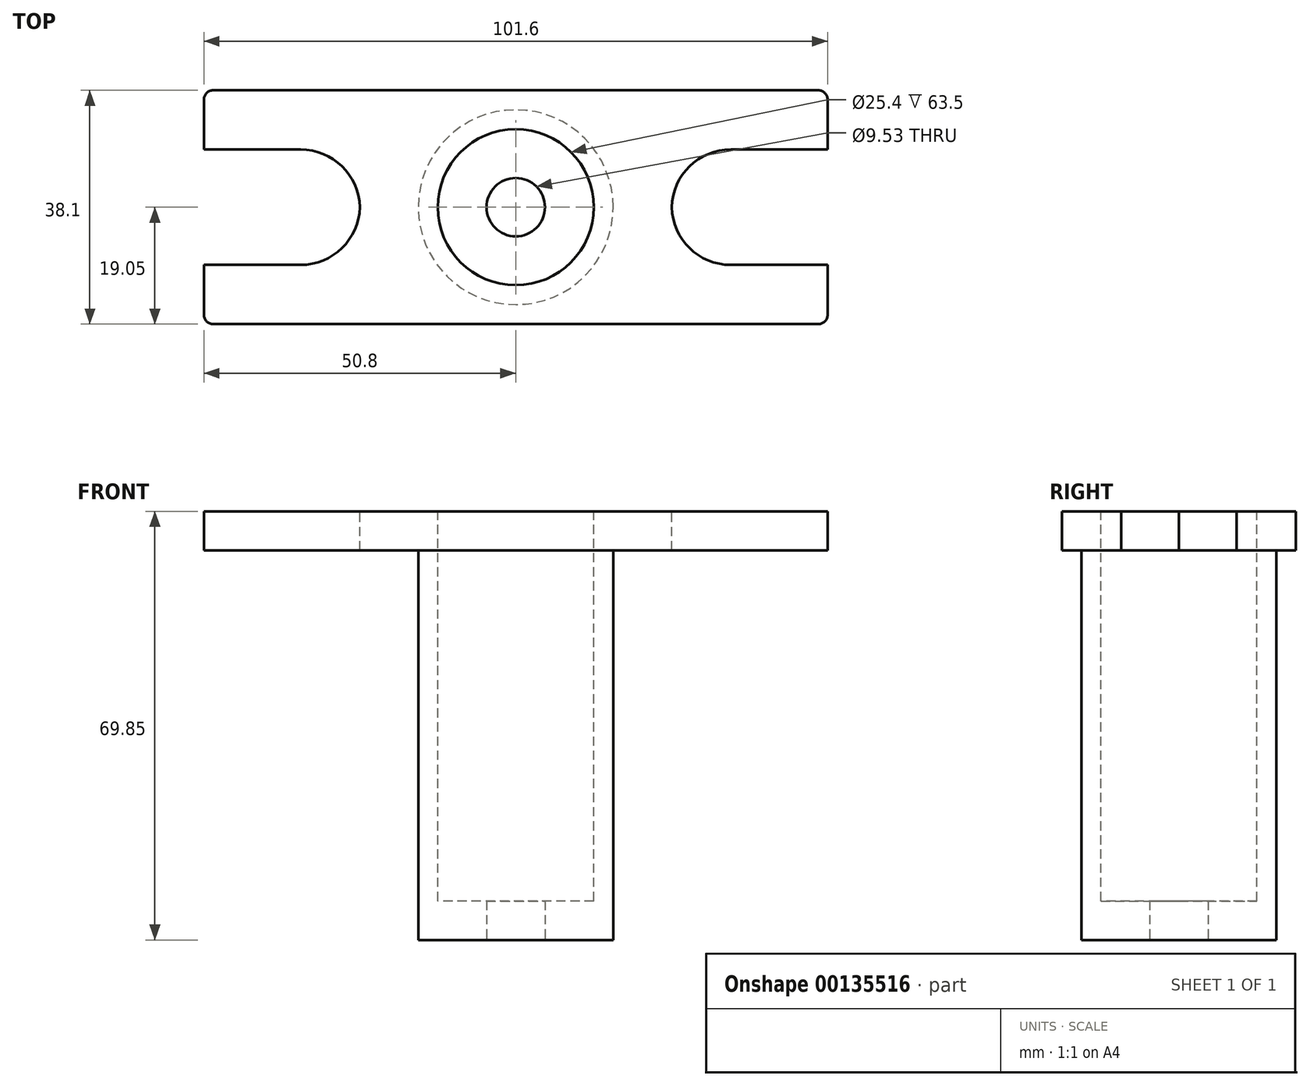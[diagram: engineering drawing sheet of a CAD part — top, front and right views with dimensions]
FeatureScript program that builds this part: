
annotation { "Feature Type Name" : "Feature", "Feature Type Description" : "" }
export const myFeature = defineFeature(function(context is Context, id is Id, definition is map)
    precondition{}
    {
        {
            var Q0;
            Q0=qCreatedBy(makeId("Top.planeOp"),FACE);
            var sketch = newSketch(context, id + "F0", { "sketchPlane" : qUnion([Q0])});
            skCircle(sketch, "E0", {"center": v(0, 0) * mm, "radius": 12.7 * mm});
            skLineSegment(sketch, "E1", {"start": v(49.28, 19.05) * mm, "end": v(-49.28, 19.05) * mm});
            skLineSegment(sketch, "E2", {"start": v(-50.8, 17.53) * mm, "end": v(-50.8, 9.4) * mm});
            skLineSegment(sketch, "E3", {"start": v(-50.8, 9.4) * mm, "end": v(-35.05, 9.4) * mm});
            skLineSegment(sketch, "E4", {"start": v(-25.4, 0) * mm, "end": v(-25.4, -0.25) * mm});
            skLineSegment(sketch, "E5", {"start": v(-25.4, 0.25) * mm, "end": v(-25.4, 0) * mm});
            skLineSegment(sketch, "E6", {"start": v(-35.05, -9.4) * mm, "end": v(-50.8, -9.4) * mm});
            skLineSegment(sketch, "E7", {"start": v(-50.8, -9.4) * mm, "end": v(-50.8, -17.53) * mm});
            skLineSegment(sketch, "E8", {"start": v(-49.28, -19.05) * mm, "end": v(49.28, -19.05) * mm});
            skLineSegment(sketch, "E9", {"start": v(50.8, -17.53) * mm, "end": v(50.8, -9.4) * mm});
            skLineSegment(sketch, "E10", {"start": v(50.8, -9.4) * mm, "end": v(35.05, -9.4) * mm});
            skLineSegment(sketch, "E11", {"start": v(25.4, -0.25) * mm, "end": v(25.4, 0.25) * mm});
            skLineSegment(sketch, "E12", {"start": v(35.05, 9.4) * mm, "end": v(50.8, 9.4) * mm});
            skLineSegment(sketch, "E13", {"start": v(50.8, 9.4) * mm, "end": v(50.8, 17.53) * mm});
            skPoint(sketch, "E14", {"position": v(25.4, 0) * mm});
            skPoint(sketch, "E15.visualSharp", {"position": v(-25.4, 9.4) * mm});
            skArc(sketch, "E15.filletArc", {"start": v(-25.4, -0.25) * mm, "mid": v(-28.23, 6.57) * mm, "end": v(-35.05, 9.4) * mm});
            skPoint(sketch, "E16.visualSharp", {"position": v(-25.4, -9.4) * mm});
            skArc(sketch, "E16.filletArc", {"start": v(-35.05, -9.4) * mm, "mid": v(-28.23, -6.57) * mm, "end": v(-25.4, 0.25) * mm});
            skPoint(sketch, "E17.visualSharp", {"position": v(25.4, 9.4) * mm});
            skArc(sketch, "E17.filletArc", {"start": v(35.05, 9.4) * mm, "mid": v(28.23, 6.57) * mm, "end": v(25.4, -0.25) * mm});
            skPoint(sketch, "E18.visualSharp", {"position": v(25.4, -9.4) * mm});
            skArc(sketch, "E18.filletArc", {"start": v(25.4, 0.25) * mm, "mid": v(28.23, -6.57) * mm, "end": v(35.05, -9.4) * mm});
            skPoint(sketch, "E19.visualSharp", {"position": v(50.8, 19.05) * mm});
            skArc(sketch, "E19.filletArc", {"start": v(50.8, 17.53) * mm, "mid": v(50.35, 18.6) * mm, "end": v(49.28, 19.05) * mm});
            skPoint(sketch, "E20.visualSharp", {"position": v(50.8, -19.05) * mm});
            skArc(sketch, "E20.filletArc", {"start": v(49.28, -19.05) * mm, "mid": v(50.35, -18.6) * mm, "end": v(50.8, -17.53) * mm});
            skPoint(sketch, "E21.visualSharp", {"position": v(-50.8, -19.05) * mm});
            skArc(sketch, "E21.filletArc", {"start": v(-50.8, -17.53) * mm, "mid": v(-50.35, -18.6) * mm, "end": v(-49.28, -19.05) * mm});
            skPoint(sketch, "E22.visualSharp", {"position": v(-50.8, 19.05) * mm});
            skArc(sketch, "E22.filletArc", {"start": v(-49.28, 19.05) * mm, "mid": v(-50.35, 18.6) * mm, "end": v(-50.8, 17.53) * mm});
            skSolve(sketch);
        }
        {
            var Q0;
            Q0 = qSketchRegion(id + "F0", true);
            extrude(context, id + "F1", {"entities" : qUnion([Q0]), "oppositeDirection" : true, "depth" : 6.35 * mm});
        }
        {
            var Q0;
            Q0=makeQuery(id+"F1.opExtrude","CAP_FACE",FACE,{"disambiguationData":[OSD([sQuery(id+"F0.wireOp",EDGE,"E0"),sQuery(id+"F0.wireOp",EDGE,"E1"),sQuery(id+"F0.wireOp",EDGE,"E2"),sQuery(id+"F0.wireOp",EDGE,"E3"),sQuery(id+"F0.wireOp",EDGE,"E6"),sQuery(id+"F0.wireOp",EDGE,"E7"),sQuery(id+"F0.wireOp",EDGE,"E8"),sQuery(id+"F0.wireOp",EDGE,"E9"),sQuery(id+"F0.wireOp",EDGE,"E10"),sQuery(id+"F0.wireOp",EDGE,"E12"),sQuery(id+"F0.wireOp",EDGE,"E13"),sQuery(id+"F0.wireOp",EDGE,"E15.filletArc"),sQuery(id+"F0.wireOp",EDGE,"E16.filletArc"),sQuery(id+"F0.wireOp",EDGE,"E17.filletArc"),sQuery(id+"F0.wireOp",EDGE,"E18.filletArc"),sQuery(id+"F0.wireOp",EDGE,"E19.filletArc"),sQuery(id+"F0.wireOp",EDGE,"E20.filletArc"),sQuery(id+"F0.wireOp",EDGE,"E21.filletArc"),sQuery(id+"F0.wireOp",EDGE,"E22.filletArc")])],"isStart":false});
            var sketch = newSketch(context, id + "F2", { "sketchPlane" : qUnion([Q0])});
            skCircle(sketch, "E23.0", {"center": v(0, 0) * mm, "radius": 12.7 * mm});
            skCircle(sketch, "E24", {"center": v(0, 0) * mm, "radius": 15.88 * mm});
            skSolve(sketch);
        }
        {
            var Q0;
            Q0 = qSketchRegion(id + "F2", true);
            extrude(context, id + "F3", {"entities" : qUnion([Q0]), "operationType" : NewBodyOperationType.ADD, "depth" : 57.15 * mm});
        }
        {
            var Q0;
            Q0=makeQuery(id+"F3.opExtrude","CAP_FACE",FACE,{"disambiguationData":[OSD([sQuery(id+"F2.wireOp",EDGE,"E23.0"),sQuery(id+"F2.wireOp",EDGE,"E24")])],"isStart":false});
            var sketch = newSketch(context, id + "F4", { "sketchPlane" : qUnion([Q0])});
            skCircle(sketch, "E25.0", {"center": v(0, 0) * mm, "radius": 15.88 * mm});
            skSolve(sketch);
        }
        {
            var Q0;
            Q0 = qSketchRegion(id + "F4", true);
            extrude(context, id + "F5", {"entities" : qUnion([Q0]), "operationType" : NewBodyOperationType.ADD, "depth" : 6.35 * mm});
        }
        {
            var Q0;
            Q0=makeQuery(id+"F5.opExtrude","CAP_FACE",FACE,{"disambiguationData":[OSD([sQuery(id+"F4.wireOp",EDGE,"E25.0")])],"isStart":false});
            var sketch = newSketch(context, id + "F6", { "sketchPlane" : qUnion([Q0])});
            skCircle(sketch, "E26", {"center": v(0, 0) * mm, "radius": 4.76 * mm});
            skSolve(sketch);
        }
        {
            var Q0;
            Q0 = qSketchRegion(id + "F6", true);
            extrude(context, id + "F7", {"entities" : qUnion([Q0]), "operationType" : NewBodyOperationType.REMOVE, "endBound" : BoundingType.THROUGH_ALL, "oppositeDirection" : true, "depth" : 25.4 * mm});
        }
    });
